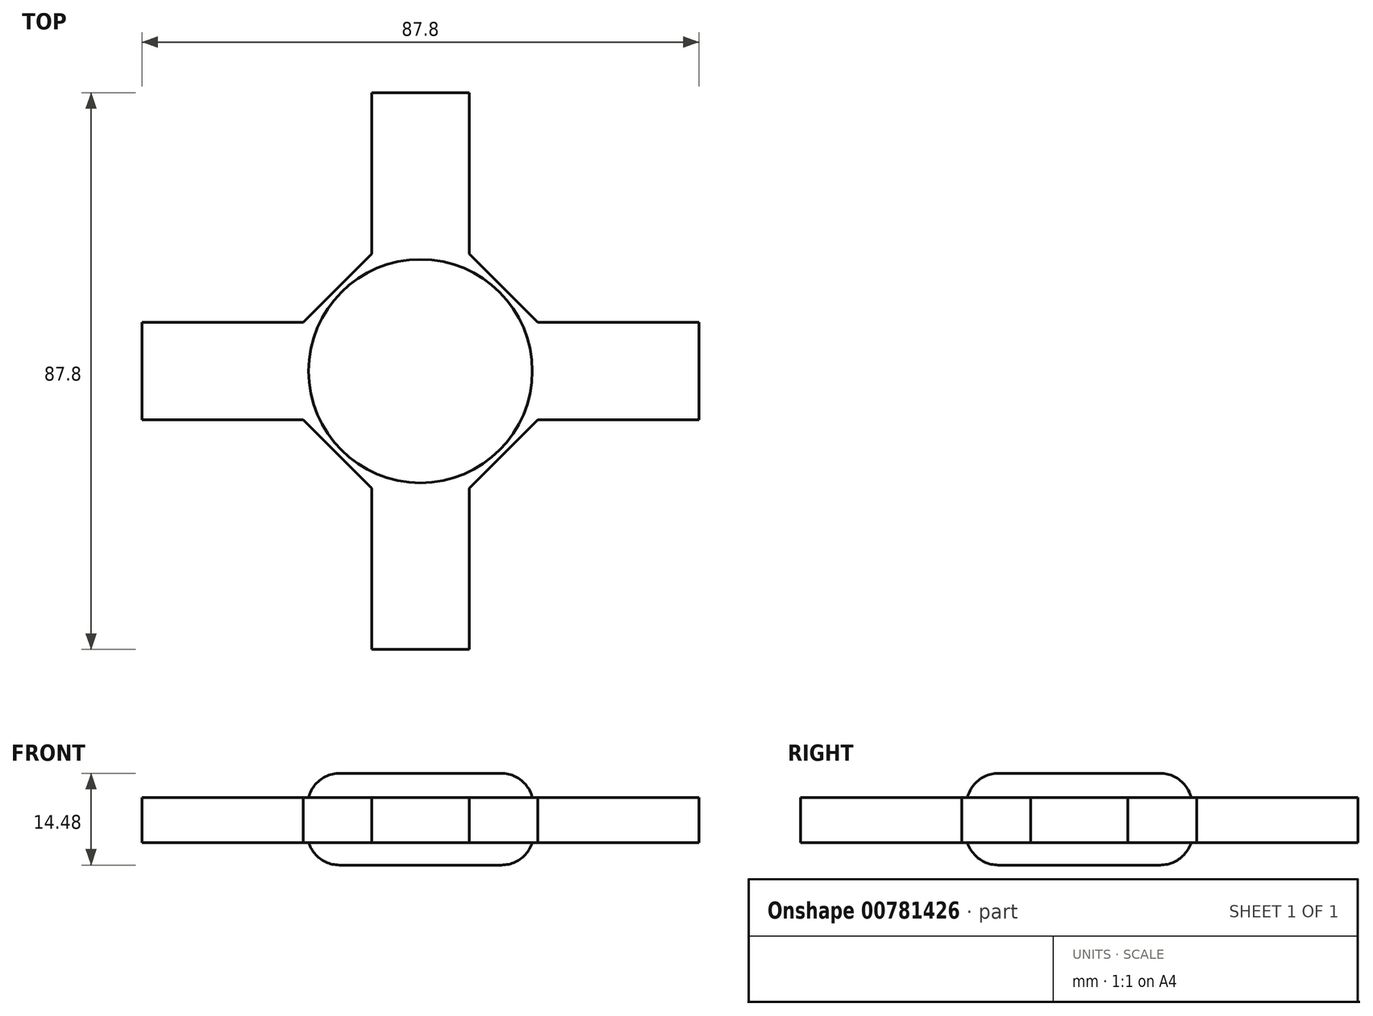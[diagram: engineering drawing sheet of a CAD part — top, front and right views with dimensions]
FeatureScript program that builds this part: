
annotation { "Feature Type Name" : "Feature", "Feature Type Description" : "" }
export const myFeature = defineFeature(function(context is Context, id is Id, definition is map)
    precondition{}
    {
        {
            var Q0;
            Q0=qCreatedBy(makeId("Top.planeOp"),FACE);
            var sketch = newSketch(context, id + "F0", { "sketchPlane" : qUnion([Q0])});
            skCircle(sketch, "E0.cCircle", {"center": v(0, 0) * mm, "radius": 18.5 * mm, "construction": true});
            skLineSegment(sketch, "E0.0", {"start": v(-7.66, 18.5) * mm, "end": v(7.66, 18.5) * mm});
            skLineSegment(sketch, "E0.1", {"start": v(7.66, 18.5) * mm, "end": v(18.5, 7.66) * mm});
            skLineSegment(sketch, "E0.2", {"start": v(18.5, 7.66) * mm, "end": v(18.5, -7.66) * mm});
            skLineSegment(sketch, "E0.3", {"start": v(18.5, -7.66) * mm, "end": v(7.66, -18.5) * mm});
            skLineSegment(sketch, "E0.4", {"start": v(7.66, -18.5) * mm, "end": v(-7.66, -18.5) * mm});
            skLineSegment(sketch, "E0.5", {"start": v(-7.66, -18.5) * mm, "end": v(-18.5, -7.66) * mm});
            skLineSegment(sketch, "E0.6", {"start": v(-18.5, -7.66) * mm, "end": v(-18.5, 7.66) * mm});
            skLineSegment(sketch, "E0.7", {"start": v(-18.5, 7.66) * mm, "end": v(-7.66, 18.5) * mm});
            skPoint(sketch, "E0.0.midPoint", {"position": v(0, 18.5) * mm});
            skSolve(sketch);
        }
        {
            var Q0;
            Q0 = qSketchRegion(id + "F0", true);
            extrude(context, id + "F1", {"entities" : qUnion([Q0]), "depth" : 7.11 * mm, "offsetDistance" : 25.4 * mm});
        }
        {
            var Q0;
            Q0=makeQuery(id+"F1.opExtrude","SWEPT_FACE",FACE,{"disambiguationData":[OSD([sQuery(id+"F0.wireOp",EDGE,"E0.4")])]});
            extrude(context, id + "F2", {"entities" : qUnion([Q0]), "operationType" : NewBodyOperationType.ADD, "depth" : 25.4 * mm, "offsetDistance" : 25.4 * mm});
        }
        {
            var Q0;
            Q0=makeQuery(id+"F1.opExtrude","SWEPT_FACE",FACE,{"disambiguationData":[OSD([sQuery(id+"F0.wireOp",EDGE,"E0.6")])]});
            extrude(context, id + "F3", {"entities" : qUnion([Q0]), "operationType" : NewBodyOperationType.ADD, "depth" : 25.4 * mm, "offsetDistance" : 25.4 * mm});
        }
        {
            var Q0;
            Q0=makeQuery(id+"F1.opExtrude","SWEPT_FACE",FACE,{"disambiguationData":[OSD([sQuery(id+"F0.wireOp",EDGE,"E0.0")])]});
            extrude(context, id + "F4", {"entities" : qUnion([Q0]), "operationType" : NewBodyOperationType.ADD, "depth" : 25.4 * mm, "offsetDistance" : 25.4 * mm});
        }
        {
            var Q0;
            Q0=makeQuery(id+"F1.opExtrude","SWEPT_FACE",FACE,{"disambiguationData":[OSD([sQuery(id+"F0.wireOp",EDGE,"E0.2")])]});
            extrude(context, id + "F5", {"entities" : qUnion([Q0]), "operationType" : NewBodyOperationType.ADD, "depth" : 25.4 * mm, "offsetDistance" : 25.4 * mm});
        }
        {
            var Q0;
            Q0=qCreatedBy(makeId("Top.planeOp"),FACE);
            var sketch = newSketch(context, id + "F6", { "sketchPlane" : qUnion([Q0])});
            skCircle(sketch, "E1", {"center": v(0, 0) * mm, "radius": 17.62 * mm});
            skSolve(sketch);
        }
        {
            var Q0;
            Q0 = qSketchRegion(id + "F6", true);
            extrude(context, id + "F7", {"entities" : qUnion([Q0]), "operationType" : NewBodyOperationType.ADD, "depth" : 10.92 * mm, "offsetDistance" : 25.4 * mm});
        }
        {
            var Q0;
            Q0 = qSketchRegion(id + "F6", true);
            extrude(context, id + "F8", {"entities" : qUnion([Q0]), "operationType" : NewBodyOperationType.ADD, "oppositeDirection" : true, "depth" : 3.56 * mm, "offsetDistance" : 25.4 * mm});
        }
        {
            var Q0;
            Q0=makeQuery(id+"F7.opExtrude","CAP_FACE",FACE,{"disambiguationData":[OSD([sQuery(id+"F6.wireOp",EDGE,"E1")])],"isStart":false});
            fillet(context, id + "F9", {"entities" : qUnion([Q0]), "radius" : 5.08 * mm, "tangentPropagation" : true, "allowEdgeOverflow" : false});
        }
        {
            var Q0;
            Q0=makeQuery(id+"F8.opExtrude","CAP_FACE",FACE,{"disambiguationData":[OSD([sQuery(id+"F6.wireOp",EDGE,"E1")])],"isStart":false});
            fillet(context, id + "F10", {"entities" : qUnion([Q0]), "radius" : 5.08 * mm, "tangentPropagation" : true, "allowEdgeOverflow" : false});
        }
    });
